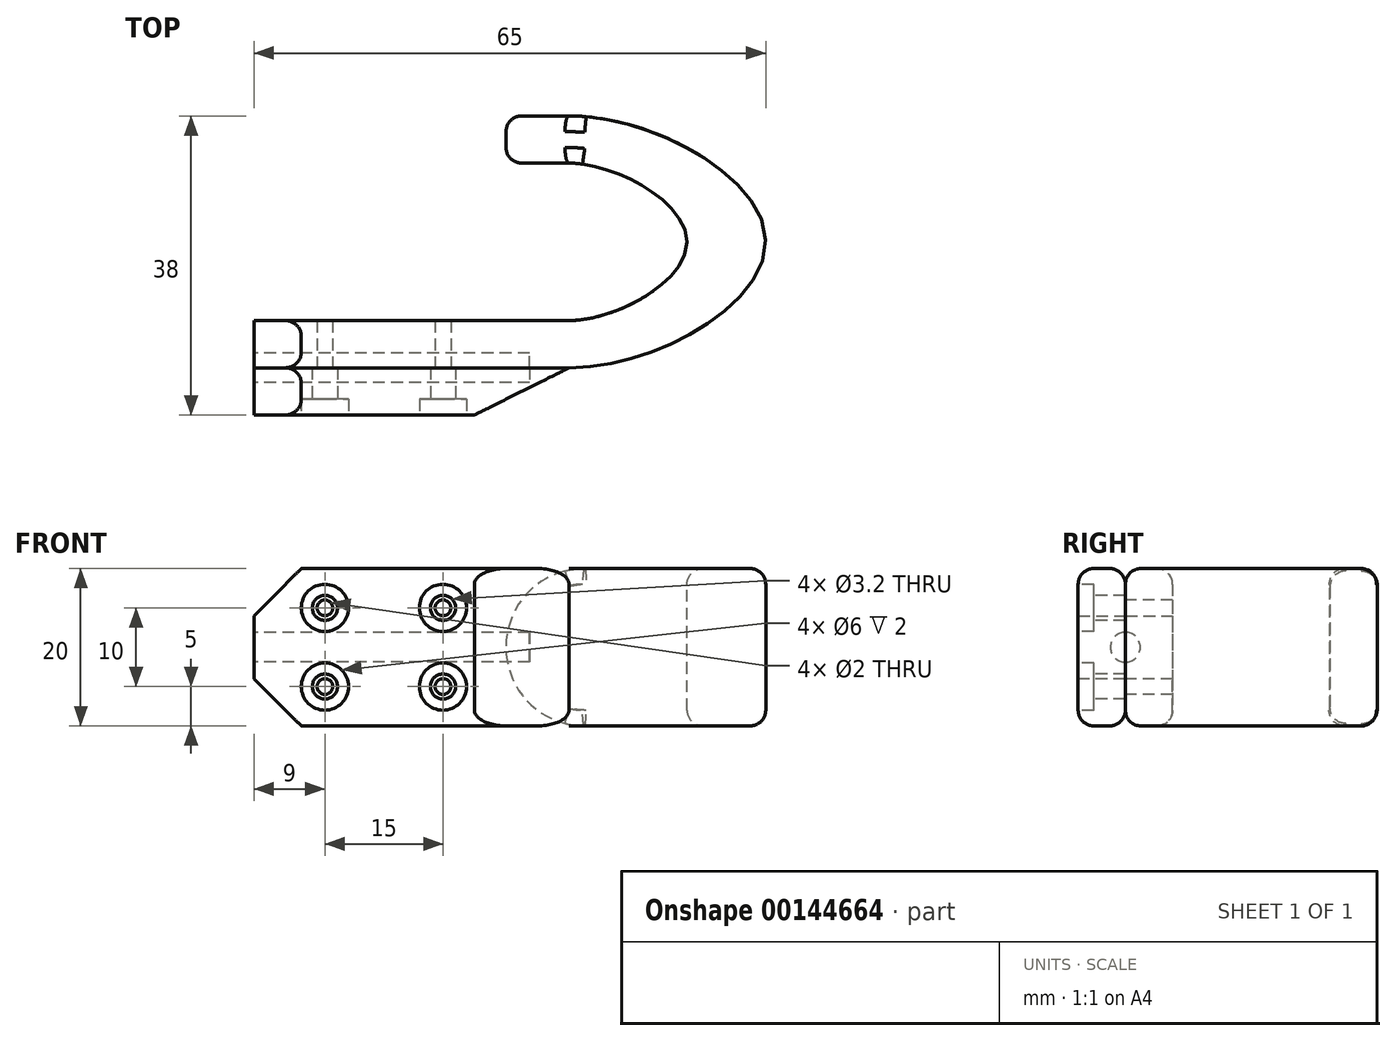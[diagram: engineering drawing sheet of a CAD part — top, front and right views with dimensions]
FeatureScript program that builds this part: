
annotation { "Feature Type Name" : "Feature", "Feature Type Description" : "" }
export const myFeature = defineFeature(function(context is Context, id is Id, definition is map)
    precondition{}
    {
        {
            var Q0;
            Q0=qCreatedBy(makeId("Top.planeOp"),FACE);
            var sketch = newSketch(context, id + "F0", { "sketchPlane" : qUnion([Q0])});
            skLineSegment(sketch, "E0", {"start": v(0, 0) * mm, "end": v(40, 0) * mm});
            skLineSegment(sketch, "E1", {"start": v(0, 0) * mm, "end": v(0, 6) * mm});
            skLineSegment(sketch, "E2", {"start": v(0, 6) * mm, "end": v(40, 6) * mm});
            skLineSegment(sketch, "E3", {"start": v(40, 6) * mm, "end": v(40, 16) * mm});
            skLineSegment(sketch, "E4", {"start": v(40, 32) * mm, "end": v(32, 32) * mm});
            skLineSegment(sketch, "E5", {"start": v(32, 32) * mm, "end": v(32, 26) * mm});
            skLineSegment(sketch, "E6", {"start": v(32, 26) * mm, "end": v(40, 26) * mm});
            skPoint(sketch, "E7.1.internal.snap0", {"position": v(55, 16) * mm});
            skFitSpline(sketch, "E7", {"points": [v(40, 32) * mm, v(65, 16) * mm, v(40, 0) * mm], "startDerivative": vector(66, 0) * mm, "endDerivative": vector(-66, 0) * mm});
            skFitSpline(sketch, "E8", {"points": [v(40, 26) * mm, v(55, 16) * mm, v(40, 6) * mm], "startDerivative": vector(36, 0) * mm, "endDerivative": vector(-36, 0) * mm});
            skSolve(sketch);
        }
        {
            var Q0;
            Q0=makeQuery(id+"F0.imprint","IMPRINT",FACE,{"disambiguationData":[TD([[makeQuery(id+"F0.imprint","IMPRINT",EDGE,{"derivedFrom":sQuery(id+"F0.wireOp",EDGE,"E0")}),1.0]])]});
            extrude(context, id + "F1", {"entities" : qUnion([Q0]), "depth" : 20 * mm});
        }
        {
            var Q0;
            Q0=makeQuery(id+"F1.opExtrude","CAP_EDGE",EDGE,{"disambiguationData":[OSD([sQuery(id+"F0.wireOp",EDGE,"E5")])],"isStart":true});
            var Q1;
            Q1=makeQuery(id+"F1.opExtrude","CAP_EDGE",EDGE,{"disambiguationData":[OSD([sQuery(id+"F0.wireOp",EDGE,"E5")])],"isStart":false});
            fillet(context, id + "F2", {"entities" : qUnion([Q0, Q1]), "radius" : 10 * mm, "tangentPropagation" : true, "allowEdgeOverflow" : false});
        }
        {
            var Q0;
            Q0=makeQuery(id+"F1.opExtrude","CAP_EDGE",EDGE,{"disambiguationData":[OSD([sQuery(id+"F0.wireOp",EDGE,"E2")])],"isStart":true});
            var Q1;
            Q1=makeQuery(id+"F1.opExtrude","CAP_EDGE",EDGE,{"disambiguationData":[OSD([sQuery(id+"F0.wireOp",EDGE,"E0")])],"isStart":false});
            fillet(context, id + "F3", {"entities" : qUnion([Q0, Q1]), "radius" : 2 * mm, "tangentPropagation" : true, "allowEdgeOverflow" : false});
        }
        {
            var Q0;
            Q0=makeQuery(id+"F1.opExtrude","SWEPT_FACE",FACE,{"disambiguationData":[OSD([sQuery(id+"F0.wireOp",EDGE,"E1")])]});
            var sketch = newSketch(context, id + "F4", { "sketchPlane" : qUnion([Q0])});
            skCircle(sketch, "E9", {"center": v(0, 10) * mm, "radius": 1.9 * mm});
            skLineSegment(sketch, "E10.bottom", {"start": v(0, 0) * mm, "end": v(6, 0) * mm});
            skLineSegment(sketch, "E10.top", {"start": v(0, 20) * mm, "end": v(6, 20) * mm});
            skLineSegment(sketch, "E10.left", {"start": v(0, 0) * mm, "end": v(0, 20) * mm});
            skLineSegment(sketch, "E10.right", {"start": v(6, 0) * mm, "end": v(6, 20) * mm});
            skSolve(sketch);
        }
        {
            var Q0;
            {var subQ4=sQuery(id+"F4.wireOp",EDGE,"E10.bottom");Q0=makeQuery(id+"F4.imprint","IMPRINT",FACE,{"disambiguationData":[TD([[makeQuery(id+"F4.imprint","IMPRINT",EDGE,{"derivedFrom":subQ4}),1.0]])]});}
            var Q1;
            {var subQ0=sQuery(id+"F4.wireOp",EDGE,"E10.left");var subQ1=sQuery(id+"F4.wireOp",EDGE,"E9");var subQ2=makeQuery(id+"F4.imprint","INTERSECT",VERTEX,{"disambiguationData":[OD(0.0)],"derivedFrom":[subQ1,subQ0]});Q1=makeQuery(id+"F4.imprint","IMPRINT",FACE,{"disambiguationData":[TD([[makeQuery(id+"F4.imprint","IMPRINT",EDGE,{"disambiguationData":[TD([[subQ2,1.0]])],"derivedFrom":subQ1}),1.0]])]});}
            extrude(context, id + "F5", {"entities" : qUnion([Q0, Q1]), "oppositeDirection" : true, "depth" : 40 * mm});
        }
        {
            var Q0;
            {var subQ0=sQuery(id+"F4.wireOp",EDGE,"E10.left");var subQ1=sQuery(id+"F4.wireOp",EDGE,"E9");var subQ2=makeQuery(id+"F4.imprint","INTERSECT",VERTEX,{"disambiguationData":[OD(0.0)],"derivedFrom":[subQ1,subQ0]});Q0=makeQuery(id+"F4.imprint","IMPRINT",FACE,{"disambiguationData":[TD([[makeQuery(id+"F4.imprint","IMPRINT",EDGE,{"disambiguationData":[TD([[subQ2,-1.0]])],"derivedFrom":subQ1}),1.0]])]});}
            var Q1;
            {var subQ0=sQuery(id+"F4.wireOp",EDGE,"E10.left");var subQ1=sQuery(id+"F4.wireOp",EDGE,"E9");var subQ2=makeQuery(id+"F4.imprint","INTERSECT",VERTEX,{"disambiguationData":[OD(0.0)],"derivedFrom":[subQ1,subQ0]});Q1=makeQuery(id+"F4.imprint","IMPRINT",FACE,{"disambiguationData":[TD([[makeQuery(id+"F4.imprint","IMPRINT",EDGE,{"disambiguationData":[TD([[subQ2,1.0]])],"derivedFrom":subQ1}),1.0]])]});}
            extrude(context, id + "F6", {"entities" : qUnion([Q0, Q1]), "operationType" : NewBodyOperationType.REMOVE, "oppositeDirection" : true, "depth" : 35 * mm});
        }
        {
            var Q0;
            Q0=makeQuery(id+"F5.opExtrude","SWEPT_EDGE",EDGE,{"disambiguationData":[OSD([sQuery(id+"F4.wireOp",EDGE,"E10.bottom"),sQuery(id+"F4.wireOp",EDGE,"E10.left")])]});
            var Q1;
            Q1=makeQuery(id+"F5.opExtrude","SWEPT_EDGE",EDGE,{"disambiguationData":[OSD([sQuery(id+"F4.wireOp",EDGE,"E10.bottom"),sQuery(id+"F4.wireOp",EDGE,"E10.right")])]});
            var Q2;
            Q2=makeQuery(id+"F5.opExtrude","SWEPT_EDGE",EDGE,{"disambiguationData":[OSD([sQuery(id+"F4.wireOp",EDGE,"E10.top"),sQuery(id+"F4.wireOp",EDGE,"E10.left")])]});
            var Q3;
            Q3=makeQuery(id+"F5.opExtrude","SWEPT_EDGE",EDGE,{"disambiguationData":[OSD([sQuery(id+"F4.wireOp",EDGE,"E10.top"),sQuery(id+"F4.wireOp",EDGE,"E10.right")])]});
            fillet(context, id + "F7", {"entities" : qUnion([Q0, Q1, Q2, Q3]), "radius" : 2 * mm, "tangentPropagation" : true, "allowEdgeOverflow" : false});
        }
        {
            var Q0;
            Q0=makeQuery(id+"F5.opExtrude","CAP_EDGE",EDGE,{"disambiguationData":[OSD([sQuery(id+"F4.wireOp",EDGE,"E10.right")])],"isStart":false});
            chamfer(context, id + "F8", {"entities" : qUnion([Q0]), "chamferType" : ChamferType.TWO_OFFSETS, "width1" : 12 * mm, "oppositeDirection" : false, "width2" : 6 * mm});
        }
        {
            var Q0;
            Q0=makeQuery(id+"F1.opExtrude","CAP_EDGE",EDGE,{"disambiguationData":[OSD([sQuery(id+"F0.wireOp",EDGE,"E1")])],"isStart":true});
            var Q1;
            Q1=makeQuery(id+"F5.opExtrude","CAP_EDGE",EDGE,{"disambiguationData":[OSD([sQuery(id+"F4.wireOp",EDGE,"E10.bottom")])],"isStart":true});
            var Q2;
            Q2=makeQuery(id+"F5.opExtrude","CAP_EDGE",EDGE,{"disambiguationData":[OSD([sQuery(id+"F4.wireOp",EDGE,"E10.top")])],"isStart":true});
            var Q3;
            Q3=makeQuery(id+"F1.opExtrude","CAP_EDGE",EDGE,{"disambiguationData":[OSD([sQuery(id+"F0.wireOp",EDGE,"E1")])],"isStart":false});
            chamfer(context, id + "F9", {"entities" : qUnion([Q0, Q1, Q2, Q3]), "width" : 6 * mm});
        }
        {
            var Q0;
            Q0=makeQuery(id+"F5.opExtrude","SWEPT_FACE",FACE,{"disambiguationData":[OSD([sQuery(id+"F4.wireOp",EDGE,"E10.right")])]});
            var sketch = newSketch(context, id + "F10", { "sketchPlane" : qUnion([Q0])});
            skPoint(sketch, "E11", {"position": v(9, 15) * mm});
            skPoint(sketch, "E12", {"position": v(24, 15) * mm});
            skLineSegment(sketch, "E13", {"start": v(28, 10) * mm, "end": v(0, 10) * mm});
            skPoint(sketch, "E14.MirrorP", {"position": v(24, 5) * mm});
            skPoint(sketch, "E15.MirrorP", {"position": v(9, 5) * mm});
            skSolve(sketch);
        }
        {
            var Q0;
            Q0=sQuery(id+"F10.wireOp",VERTEX,"E12");
            var Q1;
            Q1=sQuery(id+"F10.wireOp",VERTEX,"E14.MirrorP");
            var Q2;
            Q2=sQuery(id+"F10.wireOp",VERTEX,"E15.MirrorP");
            var Q3;
            Q3=sQuery(id+"F10.wireOp",VERTEX,"E11");
            var Q4;
            Q4=makeQuery(id+"F5.opExtrude","SWEPT_BODY",BODY,{"disambiguationData":[OSD([sQuery(id+"F4.wireOp",EDGE,"E10.bottom"),sQuery(id+"F4.wireOp",EDGE,"E10.top"),sQuery(id+"F4.wireOp",EDGE,"E10.left"),sQuery(id+"F4.wireOp",EDGE,"E10.right")])]});
            hole(context, id + "F11", {"style" : HoleStyle.C_BORE, "endStyle" : HoleEndStyle.BLIND, "holeDiameter" : 3.2 * mm, "cBoreDiameter" : 6 * mm, "cBoreDepth" : 2 * mm, "holeDepth" : 6 * mm, "startFromSketch" : true, "locations" : qUnion([Q0, Q1, Q2, Q3]), "scope" : qUnion([Q4])});
        }
        {
            var Q0;
            Q0=sQuery(id+"F10.wireOp",VERTEX,"E12");
            var Q1;
            Q1=sQuery(id+"F10.wireOp",VERTEX,"E14.MirrorP");
            var Q2;
            Q2=sQuery(id+"F10.wireOp",VERTEX,"E15.MirrorP");
            var Q3;
            Q3=sQuery(id+"F10.wireOp",VERTEX,"E11");
            var Q4;
            Q4=makeQuery(id+"F1.opExtrude","SWEPT_BODY",BODY,{"disambiguationData":[OSD([sQuery(id+"F0.wireOp",EDGE,"E0"),sQuery(id+"F0.wireOp",EDGE,"E1"),sQuery(id+"F0.wireOp",EDGE,"E2"),sQuery(id+"F0.wireOp",EDGE,"YuhhjfzF-jqhi-cCRV-vDRD-To9WkvO1rMDB"),sQuery(id+"F0.wireOp",EDGE,"GCBuSSMe-itzV-KpJ8-YCzT-HNt8AQCBeJfo"),sQuery(id+"F0.wireOp",EDGE,"E4"),sQuery(id+"F0.wireOp",EDGE,"E5"),sQuery(id+"F0.wireOp",EDGE,"E6")])]});
            hole(context, id + "F12", {"style" : HoleStyle.SIMPLE, "endStyle" : HoleEndStyle.BLIND, "holeDiameter" : 2 * mm, "holeDepth" : 25 * mm, "startFromSketch" : true, "locations" : qUnion([Q0, Q1, Q2, Q3]), "scope" : qUnion([Q4])});
        }
    });
